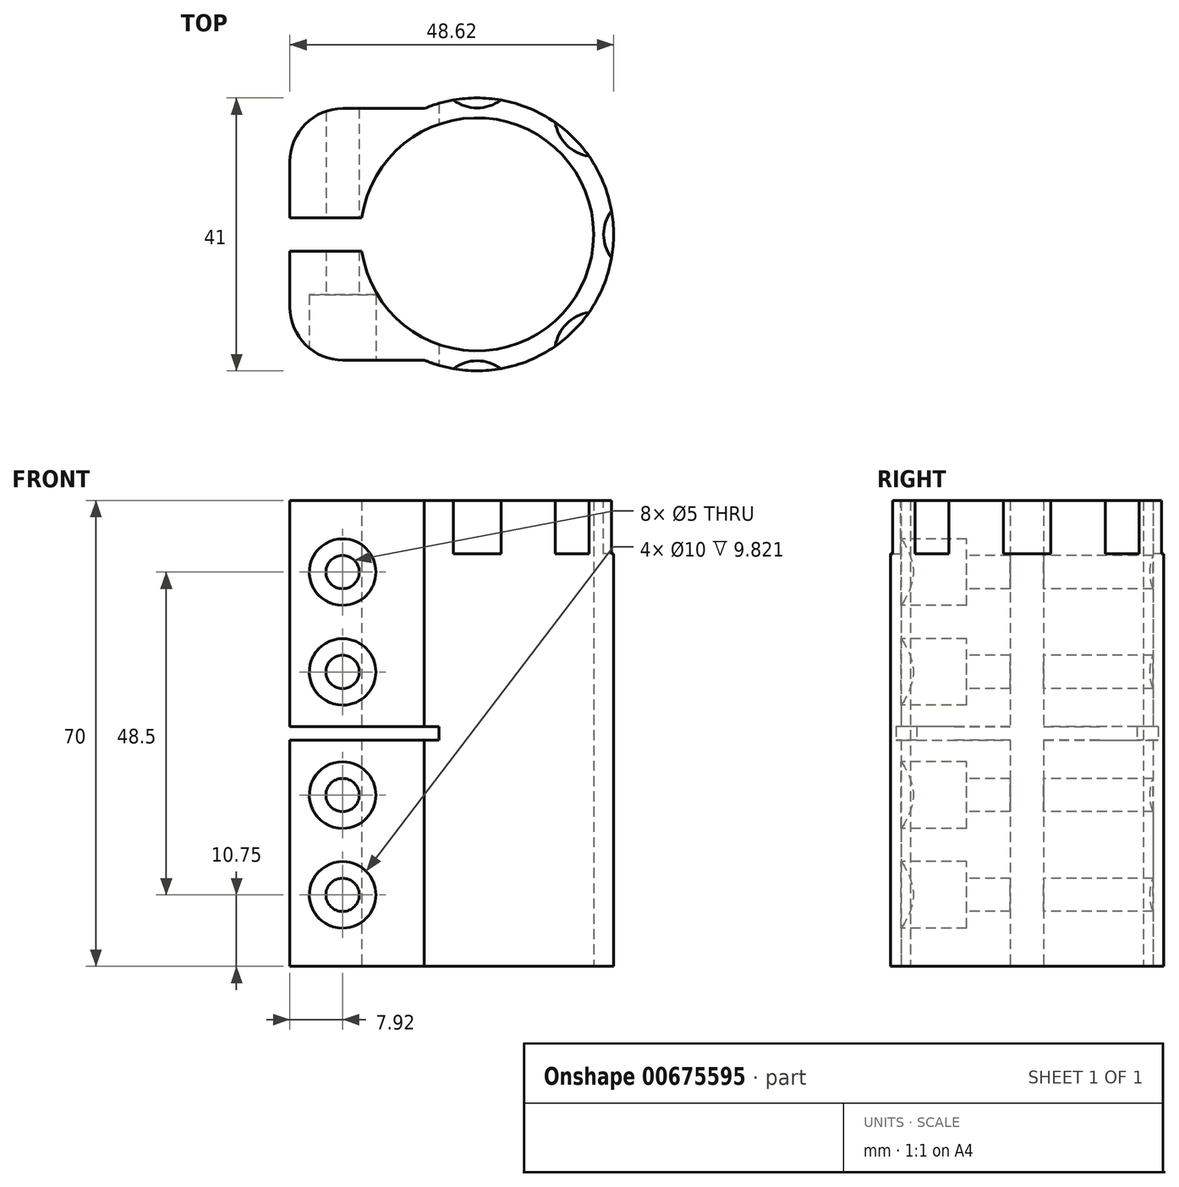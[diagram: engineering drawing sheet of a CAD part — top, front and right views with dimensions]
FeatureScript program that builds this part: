
annotation { "Feature Type Name" : "Feature", "Feature Type Description" : "" }
export const myFeature = defineFeature(function(context is Context, id is Id, definition is map)
    precondition{}
    {
        {
            var Q0;
            Q0=qCreatedBy(makeId("Top.planeOp"),FACE);
            var sketch = newSketch(context, id + "F0", { "sketchPlane" : qUnion([Q0])});
            skArc(sketch, "E0", {"start": v(-17.32, -2.5) * mm, "mid": v(17.5, 0) * mm, "end": v(-17.32, 2.5) * mm});
            skLineSegment(sketch, "E1", {"start": v(-7.92, 18.9) * mm, "end": v(-20.12, 18.9) * mm});
            skLineSegment(sketch, "E2", {"start": v(-28.12, 10.9) * mm, "end": v(-28.12, 2.5) * mm});
            skLineSegment(sketch, "E3", {"start": v(-28.12, 2.5) * mm, "end": v(-17.32, 2.5) * mm});
            skPoint(sketch, "E4.visualSharp", {"position": v(-28.12, 18.9) * mm});
            skArc(sketch, "E4.filletArc", {"start": v(-20.12, 18.9) * mm, "mid": v(-25.78, 16.57) * mm, "end": v(-28.12, 10.9) * mm});
            skLineSegment(sketch, "E5", {"start": v(0, 0) * mm, "end": v(35.68, 0) * mm, "construction": true});
            skLineSegment(sketch, "E6.MirrorCS", {"start": v(-7.92, -18.9) * mm, "end": v(-20.12, -18.9) * mm});
            skArc(sketch, "E7.MirrorCS", {"start": v(-20.12, -18.9) * mm, "mid": v(-25.78, -16.57) * mm, "end": v(-28.12, -10.9) * mm});
            skLineSegment(sketch, "E8.MirrorCS", {"start": v(-28.12, -10.9) * mm, "end": v(-28.12, -2.5) * mm});
            skLineSegment(sketch, "E9.MirrorCS", {"start": v(-28.12, -2.5) * mm, "end": v(-17.32, -2.5) * mm});
            skArc(sketch, "E10.trimOffspring", {"start": v(-7.92, -18.9) * mm, "mid": v(20.5, 0) * mm, "end": v(-7.92, 18.9) * mm});
            skSolve(sketch);
        }
        {
            var Q0;
            Q0 = qSketchRegion(id + "F0", true);
            extrude(context, id + "F1", {"entities" : qUnion([Q0]), "endBound" : BoundingType.SYMMETRIC, "depth" : 70 * mm, "offsetDistance" : 25 * mm});
        }
        {
            var Q0;
            Q0=makeQuery(id+"F1.opExtrude","SWEPT_FACE",FACE,{"disambiguationData":[OSD([sQuery(id+"F0.wireOp",EDGE,"E6.MirrorCS")])]});
            var sketch = newSketch(context, id + "F2", { "sketchPlane" : qUnion([Q0])});
            skPoint(sketch, "E11", {"position": v(-20.2, -24.25) * mm});
            skPoint(sketch, "E12", {"position": v(-20.2, -9.25) * mm});
            skPoint(sketch, "E13", {"position": v(-20.2, 9.25) * mm});
            skPoint(sketch, "E14", {"position": v(-20.2, 24.25) * mm});
            skSolve(sketch);
        }
        {
            var Q0;
            Q0=sQuery(id+"F2.wireOp",VERTEX,"E11");
            var Q1;
            Q1=sQuery(id+"F2.wireOp",VERTEX,"E12");
            var Q2;
            Q2=sQuery(id+"F2.wireOp",VERTEX,"E13");
            var Q3;
            Q3=sQuery(id+"F2.wireOp",VERTEX,"E14");
            var Q4;
            Q4=makeQuery(id+"F1.opExtrude","SWEPT_BODY",BODY,{"disambiguationData":[OSD([sQuery(id+"F0.wireOp",EDGE,"E0"),sQuery(id+"F0.wireOp",EDGE,"E1"),sQuery(id+"F0.wireOp",EDGE,"E2"),sQuery(id+"F0.wireOp",EDGE,"E3"),sQuery(id+"F0.wireOp",EDGE,"E4.filletArc"),sQuery(id+"F0.wireOp",EDGE,"E6.MirrorCS"),sQuery(id+"F0.wireOp",EDGE,"E7.MirrorCS"),sQuery(id+"F0.wireOp",EDGE,"E8.MirrorCS"),sQuery(id+"F0.wireOp",EDGE,"E9.MirrorCS"),sQuery(id+"F0.wireOp",EDGE,"E10.trimOffspring")])]});
            hole(context, id + "F3", {"style" : HoleStyle.C_BORE, "endStyle" : HoleEndStyle.THROUGH, "holeDiameter" : 5 * mm, "cBoreDiameter" : 10 * mm, "cBoreDepth" : 8 * mm, "majorDiameter" : 5 * mm, "isTappedThrough" : true, "tappedDepth" : 12 * mm, "tapClearance" : 3, "locations" : qUnion([Q0, Q1, Q2, Q3]), "scope" : qUnion([Q4])});
        }
        {
            var Q0;
            Q0=qCreatedBy(makeId("Front.planeOp"),FACE);
            var sketch = newSketch(context, id + "F4", { "sketchPlane" : qUnion([Q0])});
            skLineSegment(sketch, "E15", {"start": v(-28.12, 1) * mm, "end": v(-28.12, -1) * mm});
            skLineSegment(sketch, "E16", {"start": v(-28.12, -1) * mm, "end": v(-5.72, -1) * mm});
            skLineSegment(sketch, "E17", {"start": v(-5.72, -1) * mm, "end": v(-5.72, 1) * mm});
            skLineSegment(sketch, "E18", {"start": v(-5.72, 1) * mm, "end": v(-28.12, 1) * mm});
            skSolve(sketch);
        }
        {
            var Q0;
            Q0 = qSketchRegion(id + "F4", true);
            extrude(context, id + "F5", {"entities" : qUnion([Q0]), "operationType" : NewBodyOperationType.REMOVE, "endBound" : BoundingType.THROUGH_ALL, "oppositeDirection" : true, "depth" : 25 * mm, "offsetDistance" : 25 * mm, "hasSecondDirection" : true, "secondDirectionBound" : SecondDirectionBoundingType.THROUGH_ALL, "secondDirectionOppositeDirection" : false, "secondDirectionDepth" : 25 * mm});
        }
        {
            var Q0;
            Q0=makeQuery(id+"F1.opExtrude","CAP_FACE",FACE,{"disambiguationData":[OSD([sQuery(id+"F0.wireOp",EDGE,"E0"),sQuery(id+"F0.wireOp",EDGE,"E1"),sQuery(id+"F0.wireOp",EDGE,"E2"),sQuery(id+"F0.wireOp",EDGE,"E3"),sQuery(id+"F0.wireOp",EDGE,"E4.filletArc"),sQuery(id+"F0.wireOp",EDGE,"E6.MirrorCS"),sQuery(id+"F0.wireOp",EDGE,"E7.MirrorCS"),sQuery(id+"F0.wireOp",EDGE,"E8.MirrorCS"),sQuery(id+"F0.wireOp",EDGE,"E9.MirrorCS"),sQuery(id+"F0.wireOp",EDGE,"E10.trimOffspring")])],"isStart":false});
            var sketch = newSketch(context, id + "F6", { "sketchPlane" : qUnion([Q0])});
            skCircle(sketch, "E19", {"center": v(0, -25) * mm, "radius": 6 * mm});
            skCircle(sketch, "E20.1.0", {"center": v(17.68, -17.68) * mm, "radius": 6 * mm});
            skCircle(sketch, "E20.2.0", {"center": v(25, 0) * mm, "radius": 6 * mm});
            skCircle(sketch, "E20.3.0", {"center": v(17.68, 17.68) * mm, "radius": 6 * mm});
            skCircle(sketch, "E20.4.0", {"center": v(0, 25) * mm, "radius": 6 * mm});
            skPoint(sketch, "E20.center", {"position": v(0, 0) * mm});
            skLineSegment(sketch, "E20.anchor1", {"start": v(0, 0) * mm, "end": v(0, -25) * mm, "construction": true});
            skLineSegment(sketch, "E20.anchor2", {"start": v(0, 0) * mm, "end": v(0, 25) * mm, "construction": true});
            skSolve(sketch);
        }
        {
            var Q0;
            Q0 = qSketchRegion(id + "F6", true);
            extrude(context, id + "F7", {"entities" : qUnion([Q0]), "operationType" : NewBodyOperationType.REMOVE, "oppositeDirection" : true, "depth" : 8 * mm, "offsetDistance" : 25 * mm});
        }
    });
